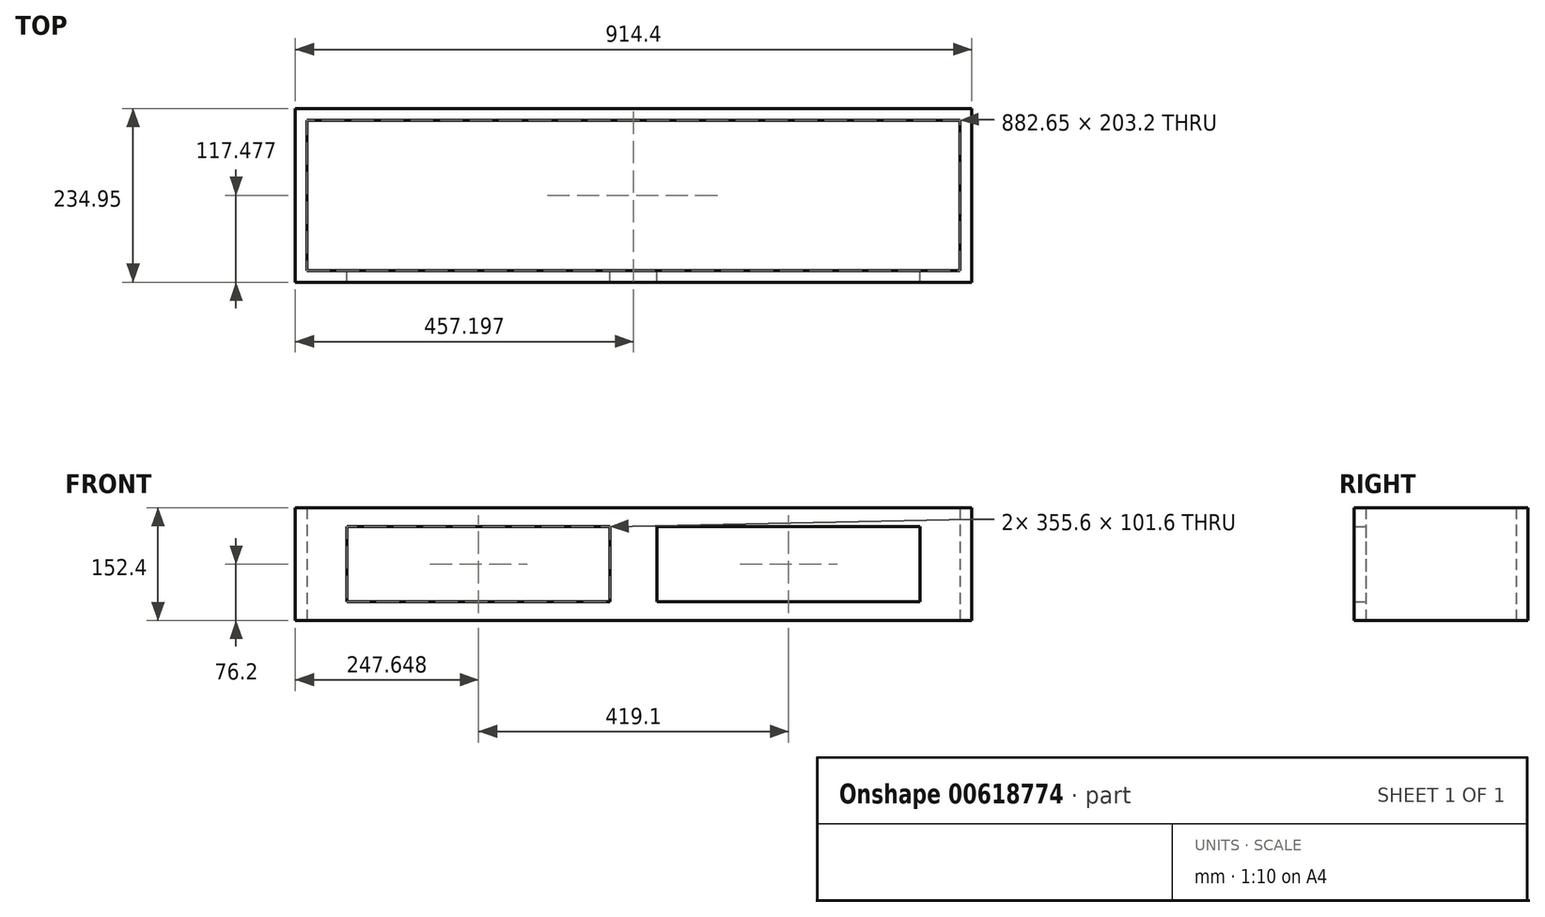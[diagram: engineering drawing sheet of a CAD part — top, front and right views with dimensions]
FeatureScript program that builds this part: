
annotation { "Feature Type Name" : "Feature", "Feature Type Description" : "" }
export const myFeature = defineFeature(function(context is Context, id is Id, definition is map)
    precondition{}
    {
        {
            var Q0;
            Q0=qCreatedBy(makeId("Top.planeOp"),FACE);
            var sketch = newSketch(context, id + "F0", { "sketchPlane" : qUnion([Q0])});
            skLineSegment(sketch, "E0.bottom", {"start": v(-466.48, 47.67) * mm, "end": v(447.92, 47.67) * mm});
            skLineSegment(sketch, "E0.top", {"start": v(-466.48, 31.8) * mm, "end": v(447.92, 31.8) * mm});
            skLineSegment(sketch, "E0.left", {"start": v(-466.48, 47.67) * mm, "end": v(-466.48, 31.8) * mm});
            skLineSegment(sketch, "E0.right", {"start": v(447.92, 47.67) * mm, "end": v(447.92, 31.8) * mm});
            skSolve(sketch);
        }
        {
            var Q0;
            Q0=makeQuery(id+"F0.imprint","IMPRINT",FACE,{"disambiguationData":[TD([[makeQuery(id+"F0.imprint","IMPRINT",EDGE,{"derivedFrom":sQuery(id+"F0.wireOp",EDGE,"E0.bottom")}),-1.0]])]});
            extrude(context, id + "F1", {"entities" : qUnion([Q0]), "depth" : 152.4 * mm, "offsetDistance" : 25.4 * mm});
        }
        {
            var Q0;
            Q0=makeQuery(id+"F1.opExtrude","SWEPT_FACE",FACE,{"disambiguationData":[OSD([sQuery(id+"F0.wireOp",EDGE,"E0.bottom")])]});
            var sketch = newSketch(context, id + "F2", { "sketchPlane" : qUnion([Q0])});
            skLineSegment(sketch, "E1.bottom", {"start": v(-378.07, 127) * mm, "end": v(-22.47, 127) * mm});
            skLineSegment(sketch, "E1.top", {"start": v(-378.07, 25.4) * mm, "end": v(-22.47, 25.4) * mm});
            skLineSegment(sketch, "E1.left", {"start": v(-378.07, 127) * mm, "end": v(-378.07, 25.4) * mm});
            skLineSegment(sketch, "E1.right", {"start": v(-22.47, 127) * mm, "end": v(-22.47, 25.4) * mm});
            skLineSegment(sketch, "E2", {"start": v(9.28, 152.4) * mm, "end": v(9.28, 0) * mm});
            skLineSegment(sketch, "E3.MirrorCS", {"start": v(396.63, 127) * mm, "end": v(41.03, 127) * mm});
            skLineSegment(sketch, "E4.MirrorCS", {"start": v(41.03, 127) * mm, "end": v(41.03, 25.4) * mm});
            skLineSegment(sketch, "E5.MirrorCS", {"start": v(396.63, 25.4) * mm, "end": v(41.03, 25.4) * mm});
            skLineSegment(sketch, "E6.MirrorCS", {"start": v(396.63, 127) * mm, "end": v(396.63, 25.4) * mm});
            skSolve(sketch);
        }
        {
            var Q0;
            Q0=makeQuery(id+"F2.imprint","IMPRINT",FACE,{"disambiguationData":[TD([[makeQuery(id+"F2.imprint","IMPRINT",EDGE,{"derivedFrom":sQuery(id+"F2.wireOp",EDGE,"E1.bottom")}),-1.0]])]});
            var Q1;
            Q1=makeQuery(id+"F2.imprint","IMPRINT",FACE,{"disambiguationData":[TD([[makeQuery(id+"F2.imprint","IMPRINT",EDGE,{"derivedFrom":sQuery(id+"F2.wireOp",EDGE,"E3.MirrorCS")}),1.0]])]});
            extrude(context, id + "F3", {"entities" : qUnion([Q0, Q1]), "operationType" : NewBodyOperationType.REMOVE, "oppositeDirection" : true, "depth" : 25.4 * mm, "offsetDistance" : 25.4 * mm});
        }
        {
            var Q0;
            Q0=makeQuery(id+"F1.opExtrude","SWEPT_FACE",FACE,{"disambiguationData":[OSD([sQuery(id+"F0.wireOp",EDGE,"E0.bottom")])]});
            var sketch = newSketch(context, id + "F4", { "sketchPlane" : qUnion([Q0])});
            skLineSegment(sketch, "E7.bottom", {"start": v(-447.92, 152.4) * mm, "end": v(-432.04, 152.4) * mm});
            skLineSegment(sketch, "E7.top", {"start": v(-447.92, 0) * mm, "end": v(-432.04, 0) * mm});
            skLineSegment(sketch, "E7.left", {"start": v(-447.92, 152.4) * mm, "end": v(-447.92, 0) * mm});
            skLineSegment(sketch, "E7.right", {"start": v(-432.04, 152.4) * mm, "end": v(-432.04, 0) * mm});
            skLineSegment(sketch, "E8.bottom", {"start": v(466.48, 152.4) * mm, "end": v(450.6, 152.4) * mm});
            skLineSegment(sketch, "E8.top", {"start": v(466.48, 0) * mm, "end": v(450.6, 0) * mm});
            skLineSegment(sketch, "E8.left", {"start": v(466.48, 152.4) * mm, "end": v(466.48, 0) * mm});
            skLineSegment(sketch, "E8.right", {"start": v(450.6, 152.4) * mm, "end": v(450.6, 0) * mm});
            skSolve(sketch);
        }
        {
            var Q0;
            Q0=makeQuery(id+"F4.imprint","IMPRINT",FACE,{"disambiguationData":[TD([[makeQuery(id+"F4.imprint","IMPRINT",EDGE,{"derivedFrom":sQuery(id+"F4.wireOp",EDGE,"E7.bottom")}),1.0]])]});
            var Q1;
            Q1=makeQuery(id+"F4.imprint","IMPRINT",FACE,{"disambiguationData":[TD([[makeQuery(id+"F4.imprint","IMPRINT",EDGE,{"derivedFrom":sQuery(id+"F4.wireOp",EDGE,"E8.bottom")}),1.0]])]});
            extrude(context, id + "F5", {"entities" : qUnion([Q0, Q1]), "operationType" : NewBodyOperationType.ADD, "depth" : 203.2 * mm, "offsetDistance" : 25.4 * mm});
        }
        {
            var Q0;
            Q0=makeQuery(id+"F5.opExtrude","CAP_FACE",FACE,{"disambiguationData":[OSD([sQuery(id+"F4.wireOp",EDGE,"E7.bottom"),sQuery(id+"F4.wireOp",EDGE,"E7.top"),sQuery(id+"F4.wireOp",EDGE,"E7.left"),sQuery(id+"F4.wireOp",EDGE,"E7.right")])],"isStart":false});
            var sketch = newSketch(context, id + "F6", { "sketchPlane" : qUnion([Q0])});
            skLineSegment(sketch, "E9.bottom", {"start": v(-447.92, 152.4) * mm, "end": v(466.48, 152.4) * mm});
            skLineSegment(sketch, "E9.top", {"start": v(-447.92, 0) * mm, "end": v(466.48, 0) * mm});
            skLineSegment(sketch, "E9.left", {"start": v(-447.92, 152.4) * mm, "end": v(-447.92, 0) * mm});
            skLineSegment(sketch, "E9.right", {"start": v(466.48, 152.4) * mm, "end": v(466.48, 0) * mm});
            skSolve(sketch);
        }
        {
            var Q0;
            {var subQ2=sQuery(id+"F6.wireOp",EDGE,"E9.right");Q0=makeQuery(id+"F6.imprint","IMPRINT",FACE,{"disambiguationData":[TD([[makeQuery(id+"F6.imprint","IMPRINT",EDGE,{"derivedFrom":subQ2}),-1.0]])]});}
            var Q1;
            {var subQ0=sQuery(id+"F6.wireOp",EDGE,"E9.left");Q1=makeQuery(id+"F6.imprint","IMPRINT",FACE,{"disambiguationData":[TD([[makeQuery(id+"F6.imprint","IMPRINT",EDGE,{"derivedFrom":subQ0}),1.0]])]});}
            extrude(context, id + "F7", {"entities" : qUnion([Q0, Q1]), "operationType" : NewBodyOperationType.ADD, "depth" : 15.88 * mm, "offsetDistance" : 25.4 * mm});
        }
    });
